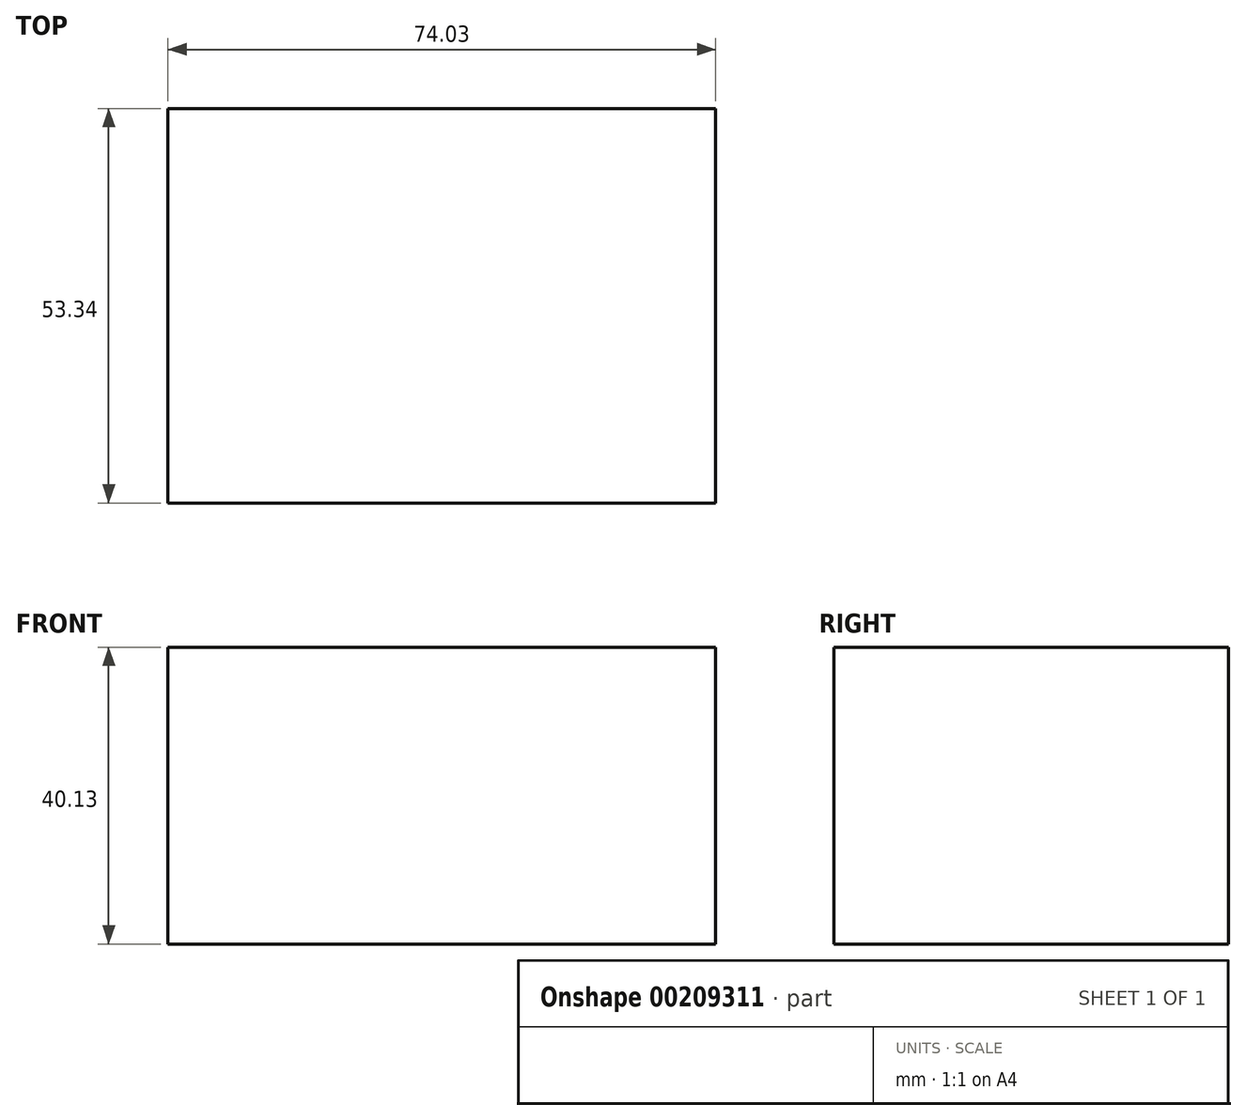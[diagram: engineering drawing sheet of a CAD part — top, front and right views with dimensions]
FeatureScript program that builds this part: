
annotation { "Feature Type Name" : "Feature", "Feature Type Description" : "" }
export const myFeature = defineFeature(function(context is Context, id is Id, definition is map)
    precondition{}
    {
        {
            var Q0;
            Q0=qCreatedBy(makeId("Top.planeOp"),FACE);
            var sketch = newSketch(context, id + "F0", { "sketchPlane" : qUnion([Q0])});
            skLineSegment(sketch, "E0.bottom", {"start": v(-24.48, 16.76) * mm, "end": v(49.55, 16.76) * mm});
            skLineSegment(sketch, "E0.top", {"start": v(-24.48, -36.58) * mm, "end": v(49.55, -36.58) * mm});
            skLineSegment(sketch, "E0.left", {"start": v(-24.48, 16.76) * mm, "end": v(-24.48, -36.58) * mm});
            skLineSegment(sketch, "E0.right", {"start": v(49.55, 16.76) * mm, "end": v(49.55, -36.58) * mm});
            skSolve(sketch);
        }
        {
            var Q0;
            Q0=makeQuery(id+"F0.imprint","IMPRINT",FACE,{"disambiguationData":[TD([[makeQuery(id+"F0.imprint","IMPRINT",EDGE,{"derivedFrom":sQuery(id+"F0.wireOp",EDGE,"E0.bottom")}),-1.0]])]});
            extrude(context, id + "F1", {"entities" : qUnion([Q0]), "depth" : 40.13 * mm});
        }
    });
